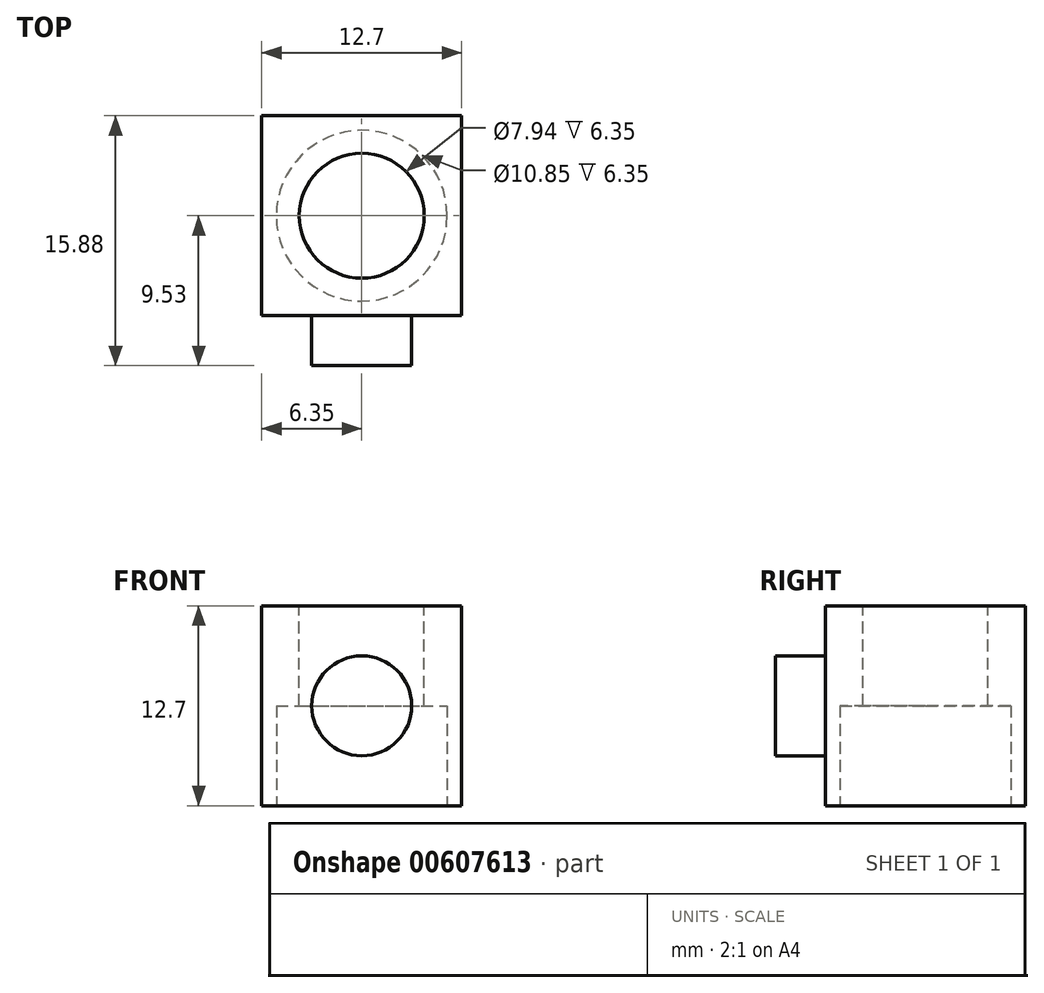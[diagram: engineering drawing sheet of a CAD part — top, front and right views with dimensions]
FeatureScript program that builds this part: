
annotation { "Feature Type Name" : "Feature", "Feature Type Description" : "" }
export const myFeature = defineFeature(function(context is Context, id is Id, definition is map)
    precondition{}
    {
        {
            var Q0;
            Q0=qCreatedBy(makeId("Top.planeOp"),FACE);
            var sketch = newSketch(context, id + "F0", { "sketchPlane" : qUnion([Q0])});
            skLineSegment(sketch, "E0.bottom", {"start": v(-6.35, 6.35) * mm, "end": v(6.35, 6.35) * mm});
            skLineSegment(sketch, "E0.top", {"start": v(-6.35, -6.35) * mm, "end": v(6.35, -6.35) * mm});
            skLineSegment(sketch, "E0.left", {"start": v(-6.35, 6.35) * mm, "end": v(-6.35, -6.35) * mm});
            skLineSegment(sketch, "E0.right", {"start": v(6.35, 6.35) * mm, "end": v(6.35, -6.35) * mm});
            skSolve(sketch);
        }
        {
            var Q0;
            Q0=makeQuery(id+"F0.imprint","IMPRINT",FACE,{"disambiguationData":[TD([[makeQuery(id+"F0.imprint","IMPRINT",EDGE,{"derivedFrom":sQuery(id+"F0.wireOp",EDGE,"E0.bottom")}),-1.0]])]});
            extrude(context, id + "F1", {"entities" : qUnion([Q0]), "depth" : 12.7 * mm, "offsetDistance" : 25.4 * mm});
        }
        {
            var Q0;
            Q0=makeQuery(id+"F1.opExtrude","CAP_FACE",FACE,{"disambiguationData":[OSD([sQuery(id+"F0.wireOp",EDGE,"E0.bottom"),sQuery(id+"F0.wireOp",EDGE,"E0.top"),sQuery(id+"F0.wireOp",EDGE,"E0.left"),sQuery(id+"F0.wireOp",EDGE,"E0.right")])],"isStart":false});
            var sketch = newSketch(context, id + "F2", { "sketchPlane" : qUnion([Q0])});
            skCircle(sketch, "E1", {"center": v(0, 0) * mm, "radius": 3.97 * mm});
            skSolve(sketch);
        }
        {
            var Q0;
            Q0 = qSketchRegion(id + "F2", true);
            extrude(context, id + "F3", {"entities" : qUnion([Q0]), "operationType" : NewBodyOperationType.REMOVE, "endBound" : BoundingType.UP_TO_NEXT, "oppositeDirection" : true, "depth" : 25.4 * mm, "offsetDistance" : 25.4 * mm});
        }
        {
            var Q0;
            Q0=makeQuery(id+"F1.opExtrude","CAP_FACE",FACE,{"disambiguationData":[OSD([sQuery(id+"F0.wireOp",EDGE,"E0.bottom"),sQuery(id+"F0.wireOp",EDGE,"E0.top"),sQuery(id+"F0.wireOp",EDGE,"E0.left"),sQuery(id+"F0.wireOp",EDGE,"E0.right")])],"isStart":true});
            var sketch = newSketch(context, id + "F4", { "sketchPlane" : qUnion([Q0])});
            skCircle(sketch, "E2", {"center": v(0, 0) * mm, "radius": 5.42 * mm});
            skSolve(sketch);
        }
        {
            var Q0;
            Q0 = qSketchRegion(id + "F4", true);
            extrude(context, id + "F5", {"entities" : qUnion([Q0]), "operationType" : NewBodyOperationType.REMOVE, "oppositeDirection" : true, "depth" : 6.35 * mm, "offsetDistance" : 25.4 * mm});
        }
        {
            var Q0;
            Q0=makeQuery(id+"F1.opExtrude","SWEPT_FACE",FACE,{"disambiguationData":[OSD([sQuery(id+"F0.wireOp",EDGE,"E0.top")])]});
            var sketch = newSketch(context, id + "F6", { "sketchPlane" : qUnion([Q0])});
            skCircle(sketch, "E3", {"center": v(0, 6.35) * mm, "radius": 3.18 * mm});
            skSolve(sketch);
        }
        {
            var Q0;
            Q0 = qSketchRegion(id + "F6", true);
            extrude(context, id + "F7", {"entities" : qUnion([Q0]), "operationType" : NewBodyOperationType.ADD, "depth" : 3.17 * mm, "offsetDistance" : 25.4 * mm});
        }
    });
